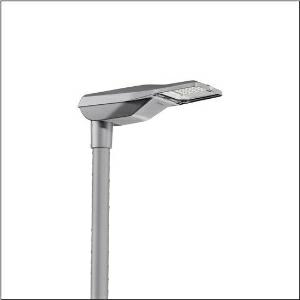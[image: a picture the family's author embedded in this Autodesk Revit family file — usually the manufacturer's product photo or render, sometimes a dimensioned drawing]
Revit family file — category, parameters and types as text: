
# Revit family: streetlight_sl_21_iq_micro___p0_8a_5xe1u31d08db_7b75
name_source: partatom
category: Lighting Fixtures
units: mm (PartAtom-declared; Revit-internal decimal feet)

## family parameters
Cut with Voids When Loaded = No
Host = Face
Light Source = No
Part Type = Normal
Room Calculation Point = No
Round Connector Dimension = Use Diameter
Shared = No

## types (1)
- --- (1 x LED, 4750 lm, 36.4 W, 3000K)
    Apparent Load = 36 VA
    CIE Flux Codes = 33 69 96 100 100
    Color Rendering = 70
    Color Temperature = 3000K
    Default Elevation = 1800 mm
    Description = Streetlight SL 21 iQ micro, mast luminaire, primary light control with lens, of PMMA, primary optical cover: cover, of toughened safety glass, transparent, light distribution: P0.8a, light emission: direct distribution, primary light characteristic: asymmetric, installation type: post-top, side-entry, LED, High Power LED, rated luminous flux: 4.750lm, luminous efficacy: 131lm/W, light colour: 730, colour temperature: 3000K, control gear: iQ-Comfort, control: pre-setting: linear dimming characteristic, Auto-Match, Temp-Guard, Lumen-Switch, Night-Set, Smart-Wire, Light-Fading, Desk-Remote (wireless, voltage-free reading and setting of iQ features in the workshop via application-optimized NFC function/RFID function), optimised constant luminous flux control (CLO 2.0), mains connection: 220..240V, AC, 50/60Hz, start of lifetime: 36W, end of service life: 38W, reduction: 16W, luminaire housing, of diecast aluminium, powder-coated, Siteco® metallic grey (DB 702S), corrosivity category C5 mid according to DIN EN ISO 12944, please order mast flange separately, inclination adjustable: 0°, 5°, 10°, 15°, sealing non-destructively replaceable, multi-level sealing system, length: 528mm, width: 235mm, height: 110mm, mast flange for spigot size: 42mm (side-entry): 5XC10008XM4, 60/48mm (side-entry/post-top): 5XC10108XM2, 76/60mm (side-entry/post-top): 5XC10108XM1, protection rating (complete): IP66, insulation class (complete): insulation class II (safety insulation), certification: CE, ENEC, ENEC+, VDE, impact resistance: IK10, permissible operating ambient temperature for outdoor applications: -40..+50°C, standard-compliant lighting for roads and squares, packaging unit: 1 piece

Light Distribution: P0.8a
    Height = 110 mm
    Lamp = 1 x LED
    Lamp Light Flux = 4750 lm
    Lamp Power = 36.4 W
    Lamp count = 1
    Length = 528 mm
    Luminous efficacy = 130 lm/W
    Manufacturer = Siteco
    ModVariant = No
    Model = 5XE1U31D08DB
    Number of Poles = 1
    OnlyDefault = Yes
    Power Factor = 1
    Product Name = Streetlight SL 21 iQ micro | P0.8a
    Product group = mast luminaire | pylon top
    ProductGroupID = 6100
    Protection Class = Protection class II
    Protection Degree = IP 66
    RLX_Detail_Level = 1
    RLX_Emergency_Light_Flux = 0 lm
    RLX_Emergency_Type = 0
    RLX_Emergency_Type_DB = No
    RlxData = <blob elided: 99189 chars, md5=92f97aa5>
    Socket = socket
    Standby Power = 0 W
    System Light Flux = 4750 lm
    System Power = 36 W
    Type Comments = factory setting: luminous flux: 100 % | dim-lin: 254 | 715 mA
    Type Image = l_1006881.jpg
    URL = http://relux.com
    VarID = @adj_094637
    Voltage = 0 V
    Weight = 0.00 kg
    Width = 235 mm

## geometry (parser evidence)
native form markers: Blend x4, Sweep x10
no freeform markers — native parametric forms only
